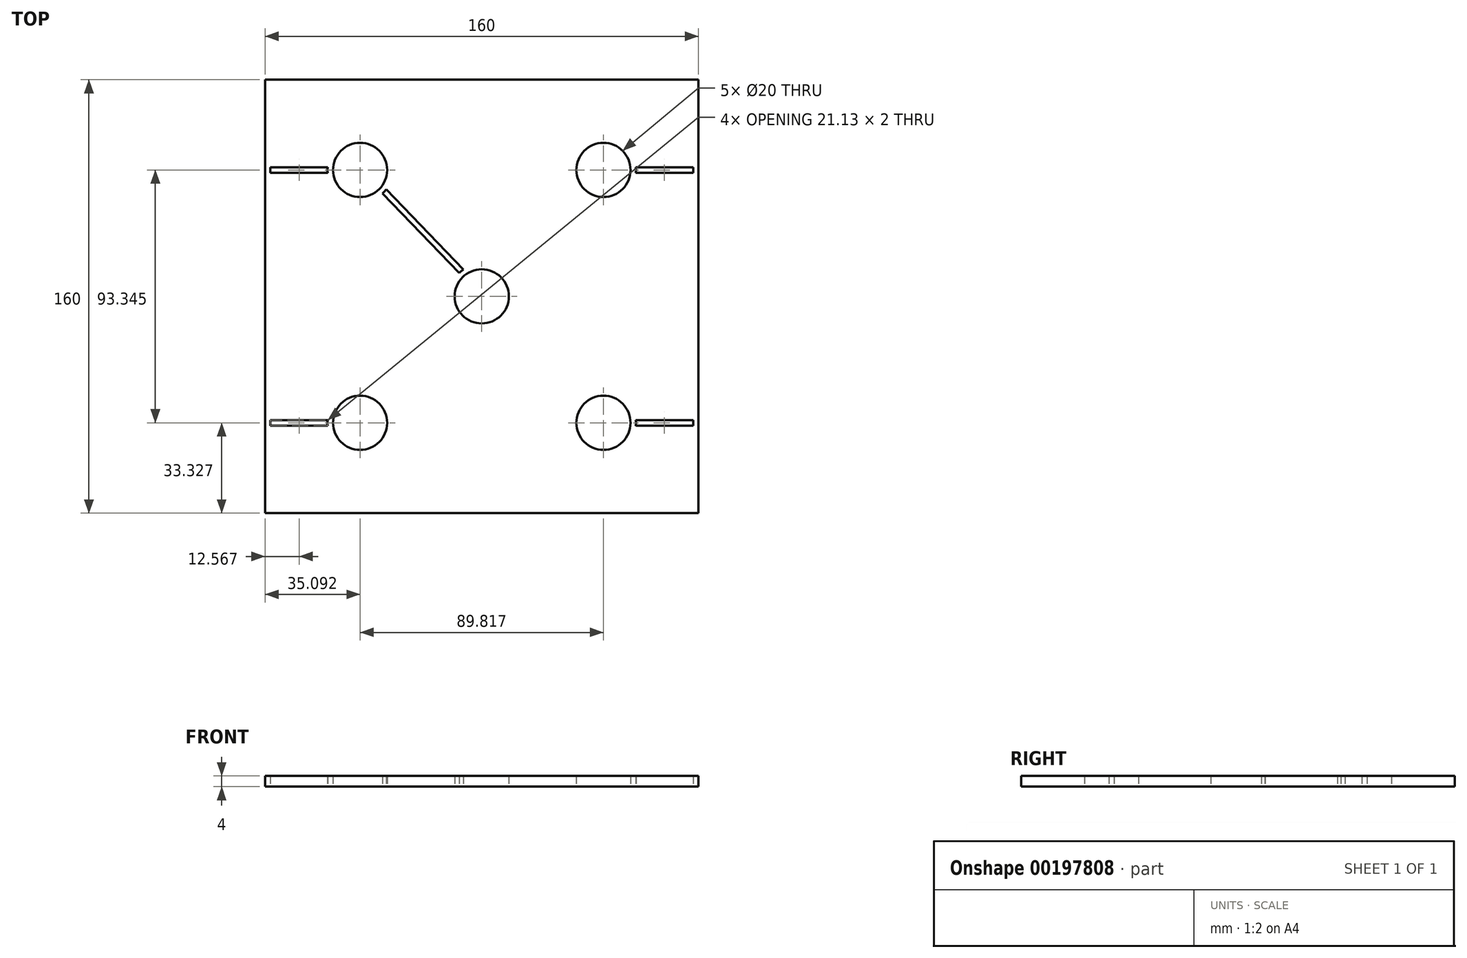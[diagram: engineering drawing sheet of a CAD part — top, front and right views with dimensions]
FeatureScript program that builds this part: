
annotation { "Feature Type Name" : "Feature", "Feature Type Description" : "" }
export const myFeature = defineFeature(function(context is Context, id is Id, definition is map)
    precondition{}
    {
        {
            var Q0;
            Q0=qCreatedBy(makeId("Top.planeOp"),FACE);
            var sketch = newSketch(context, id + "F0", { "sketchPlane" : qUnion([Q0])});
            skLineSegment(sketch, "E0.bottom", {"start": v(80, -80) * mm, "end": v(-80, -80) * mm});
            skLineSegment(sketch, "E0.top", {"start": v(80, 80) * mm, "end": v(-80, 80) * mm});
            skLineSegment(sketch, "E0.left", {"start": v(80, -80) * mm, "end": v(80, 80) * mm});
            skLineSegment(sketch, "E0.right", {"start": v(-80, -80) * mm, "end": v(-80, 80) * mm});
            skPoint(sketch, "E0.middle", {"position": v(0, 0) * mm});
            skLineSegment(sketch, "E1.bottom", {"start": v(78, -78) * mm, "end": v(-78, -78) * mm});
            skLineSegment(sketch, "E1.top", {"start": v(78, 78) * mm, "end": v(-78, 78) * mm});
            skLineSegment(sketch, "E1.left", {"start": v(78, -78) * mm, "end": v(78, 78) * mm});
            skLineSegment(sketch, "E1.right", {"start": v(-78, -78) * mm, "end": v(-78, 78) * mm});
            skCircle(sketch, "E2", {"center": v(0, 0) * mm, "radius": 10 * mm});
            skCircle(sketch, "E3", {"center": v(0, 0) * mm, "radius": 12 * mm});
            skCircle(sketch, "E4", {"center": v(-44.9, -46.67) * mm, "radius": 10 * mm});
            skCircle(sketch, "E5", {"center": v(-44.9, -46.67) * mm, "radius": 12 * mm});
            skCircle(sketch, "E6", {"center": v(44.9, -46.67) * mm, "radius": 10 * mm});
            skCircle(sketch, "E7", {"center": v(44.9, -46.67) * mm, "radius": 12 * mm});
            skCircle(sketch, "E8", {"center": v(44.9, 46.67) * mm, "radius": 10 * mm});
            skCircle(sketch, "E9", {"center": v(44.9, 46.67) * mm, "radius": 12 * mm});
            skCircle(sketch, "E10", {"center": v(-44.9, 46.67) * mm, "radius": 10 * mm});
            skCircle(sketch, "E11", {"center": v(-44.9, 46.67) * mm, "radius": 12 * mm});
            skLineSegment(sketch, "E12", {"start": v(-44.9, -46.67) * mm, "end": v(44.9, 46.67) * mm});
            skLineSegment(sketch, "E13", {"start": v(-44.9, 46.67) * mm, "end": v(44.9, -46.67) * mm});
            skArc(sketch, "E14.0.startCap", {"start": v(-46.35, 45.29) * mm, "mid": v(-46.3, 48.11) * mm, "end": v(-43.47, 48.06) * mm});
            skArc(sketch, "E14.0.endCap", {"start": v(46.35, -45.29) * mm, "mid": v(46.3, -48.11) * mm, "end": v(43.47, -48.06) * mm});
            skLineSegment(sketch, "E14.0.left", {"start": v(-43.47, 48.06) * mm, "end": v(46.35, -45.29) * mm});
            skLineSegment(sketch, "E14.0.right", {"start": v(-46.35, 45.29) * mm, "end": v(43.47, -48.06) * mm});
            skArc(sketch, "E15.0.startCap", {"start": v(-43.47, -48.06) * mm, "mid": v(-46.3, -48.11) * mm, "end": v(-46.35, -45.29) * mm});
            skArc(sketch, "E15.0.endCap", {"start": v(43.47, 48.06) * mm, "mid": v(46.3, 48.11) * mm, "end": v(46.35, 45.29) * mm});
            skLineSegment(sketch, "E15.0.left", {"start": v(-46.35, -45.29) * mm, "end": v(43.47, 48.06) * mm});
            skLineSegment(sketch, "E15.0.right", {"start": v(-43.47, -48.06) * mm, "end": v(46.35, 45.29) * mm});
            skLineSegment(sketch, "E16", {"start": v(0, -78) * mm, "end": v(0, 78) * mm, "construction": true});
            skArc(sketch, "E17.0.endCap", {"start": v(-56.9, 47.67) * mm, "mid": v(-56.89, 47.67) * mm, "end": v(-56.87, 47.67) * mm});
            skLineSegment(sketch, "E17.0.left", {"start": v(-78, 47.67) * mm, "end": v(-56.9, 47.67) * mm});
            skLineSegment(sketch, "E17.0.right", {"start": v(-78, 45.67) * mm, "end": v(-56.9, 45.67) * mm});
            skArc(sketch, "E18.0.endCap", {"start": v(56.9, 45.67) * mm, "mid": v(56.89, 45.67) * mm, "end": v(56.87, 45.67) * mm});
            skLineSegment(sketch, "E18.0.left", {"start": v(78, 45.67) * mm, "end": v(56.9, 45.67) * mm});
            skLineSegment(sketch, "E18.0.right", {"start": v(78, 47.67) * mm, "end": v(56.9, 47.67) * mm});
            skArc(sketch, "E19.0.endCap", {"start": v(56.9, -47.67) * mm, "mid": v(56.89, -47.67) * mm, "end": v(56.87, -47.67) * mm});
            skLineSegment(sketch, "E19.0.left", {"start": v(78, -47.67) * mm, "end": v(56.9, -47.67) * mm});
            skLineSegment(sketch, "E19.0.right", {"start": v(78, -45.67) * mm, "end": v(56.9, -45.67) * mm});
            skArc(sketch, "E20.0.endCap", {"start": v(-56.9, -45.67) * mm, "mid": v(-56.89, -45.67) * mm, "end": v(-56.87, -45.67) * mm});
            skLineSegment(sketch, "E20.0.left", {"start": v(-78, -45.67) * mm, "end": v(-56.9, -45.67) * mm});
            skLineSegment(sketch, "E20.0.right", {"start": v(-78, -47.67) * mm, "end": v(-56.9, -47.67) * mm});
            skArc(sketch, "E21.trimOffspring", {"start": v(-56.87, -47.67) * mm, "mid": v(-56.89, -47.67) * mm, "end": v(-56.9, -47.67) * mm});
            skPoint(sketch, "E22.MirrorCS.start.orphan", {"position": v(-78, -46.67) * mm});
            skArc(sketch, "E23.trimOffspring", {"start": v(56.87, -45.67) * mm, "mid": v(56.89, -45.67) * mm, "end": v(56.9, -45.67) * mm});
            skPoint(sketch, "E19.0.startCap.center.orphan", {"position": v(78, -46.67) * mm});
            skArc(sketch, "E24.trimOffspring", {"start": v(56.87, 47.67) * mm, "mid": v(56.89, 47.67) * mm, "end": v(56.9, 47.67) * mm});
            skPoint(sketch, "E25.start.orphan", {"position": v(78, 46.67) * mm});
            skArc(sketch, "E26.trimOffspring", {"start": v(-56.87, 45.67) * mm, "mid": v(-56.89, 45.67) * mm, "end": v(-56.9, 45.67) * mm});
            skPoint(sketch, "E17.0.startCap.center.orphan", {"position": v(-78, 46.67) * mm});
            skSolve(sketch);
        }
        {
            var Q0;
            Q0=makeQuery(id+"F0.imprint","IMPRINT",FACE,{"disambiguationData":[TD([[makeQuery(id+"F0.imprint","IMPRINT",EDGE,{"derivedFrom":sQuery(id+"F0.wireOp",EDGE,"E0.bottom")}),-1.0]])]});
            var Q1;
            Q1=makeQuery(id+"F0.imprint","IMPRINT",FACE,{"disambiguationData":[TD([[makeQuery(id+"F0.imprint","IMPRINT",EDGE,{"derivedFrom":sQuery(id+"F0.wireOp",EDGE,"E4")}),-1.0]])]});
            var Q2;
            Q2=makeQuery(id+"F0.imprint","IMPRINT",FACE,{"disambiguationData":[TD([[makeQuery(id+"F0.imprint","IMPRINT",EDGE,{"derivedFrom":sQuery(id+"F0.wireOp",EDGE,"E2")}),-1.0]])]});
            var Q3;
            Q3=makeQuery(id+"F0.imprint","IMPRINT",FACE,{"disambiguationData":[TD([[makeQuery(id+"F0.imprint","IMPRINT",EDGE,{"derivedFrom":sQuery(id+"F0.wireOp",EDGE,"E6")}),-1.0]])]});
            var Q4;
            Q4=makeQuery(id+"F0.imprint","IMPRINT",FACE,{"disambiguationData":[TD([[makeQuery(id+"F0.imprint","IMPRINT",EDGE,{"derivedFrom":sQuery(id+"F0.wireOp",EDGE,"E8")}),-1.0]])]});
            var Q5;
            Q5=makeQuery(id+"F0.imprint","IMPRINT",FACE,{"disambiguationData":[TD([[makeQuery(id+"F0.imprint","IMPRINT",EDGE,{"derivedFrom":sQuery(id+"F0.wireOp",EDGE,"E10")}),-1.0]])]});
            var Q6;
            {var subQ0=sQuery(id+"F0.wireOp",EDGE,"E13");var subQ1=sQuery(id+"F0.wireOp",EDGE,"E3");var subQ2=makeQuery(id+"F0.imprint","INTERSECT",VERTEX,{"disambiguationData":[OD(0.0)],"derivedFrom":[subQ1,subQ0]});Q6=makeQuery(id+"F0.imprint","IMPRINT",FACE,{"disambiguationData":[TD([[makeQuery(id+"F0.imprint","IMPRINT",EDGE,{"disambiguationData":[TD([[subQ2,-1.0]])],"derivedFrom":subQ1}),-1.0]])]});}
            var Q7;
            {var subQ0=sQuery(id+"F0.wireOp",EDGE,"E14.0.left");var subQ1=sQuery(id+"F0.wireOp",EDGE,"E3");var subQ2=makeQuery(id+"F0.imprint","INTERSECT",VERTEX,{"disambiguationData":[OD(0.0)],"derivedFrom":[subQ1,subQ0]});Q7=makeQuery(id+"F0.imprint","IMPRINT",FACE,{"disambiguationData":[TD([[makeQuery(id+"F0.imprint","IMPRINT",EDGE,{"disambiguationData":[TD([[subQ2,-1.0]])],"derivedFrom":subQ1}),-1.0]])]});}
            var Q8;
            {var subQ0=sQuery(id+"F0.wireOp",EDGE,"E15.0.left");var subQ1=sQuery(id+"F0.wireOp",EDGE,"E3");var subQ2=makeQuery(id+"F0.imprint","INTERSECT",VERTEX,{"disambiguationData":[OD(1.0)],"derivedFrom":[subQ1,subQ0]});Q8=makeQuery(id+"F0.imprint","IMPRINT",FACE,{"disambiguationData":[TD([[makeQuery(id+"F0.imprint","IMPRINT",EDGE,{"disambiguationData":[TD([[subQ2,-1.0]])],"derivedFrom":subQ1}),-1.0]])]});}
            var Q9;
            {var subQ0=sQuery(id+"F0.wireOp",EDGE,"E12");var subQ1=sQuery(id+"F0.wireOp",EDGE,"E3");var subQ2=makeQuery(id+"F0.imprint","INTERSECT",VERTEX,{"disambiguationData":[OD(1.0)],"derivedFrom":[subQ1,subQ0]});Q9=makeQuery(id+"F0.imprint","IMPRINT",FACE,{"disambiguationData":[TD([[makeQuery(id+"F0.imprint","IMPRINT",EDGE,{"disambiguationData":[TD([[subQ2,-1.0]])],"derivedFrom":subQ1}),-1.0]])]});}
            var Q10;
            {var subQ0=sQuery(id+"F0.wireOp",EDGE,"E14.0.right");var subQ1=sQuery(id+"F0.wireOp",EDGE,"E3");var subQ2=makeQuery(id+"F0.imprint","INTERSECT",VERTEX,{"disambiguationData":[OD(1.0)],"derivedFrom":[subQ1,subQ0]});Q10=makeQuery(id+"F0.imprint","IMPRINT",FACE,{"disambiguationData":[TD([[makeQuery(id+"F0.imprint","IMPRINT",EDGE,{"disambiguationData":[TD([[subQ2,-1.0]])],"derivedFrom":subQ1}),-1.0]])]});}
            var Q11;
            {var subQ0=sQuery(id+"F0.wireOp",EDGE,"E13");var subQ1=sQuery(id+"F0.wireOp",EDGE,"E3");var subQ2=makeQuery(id+"F0.imprint","INTERSECT",VERTEX,{"disambiguationData":[OD(1.0)],"derivedFrom":[subQ1,subQ0]});Q11=makeQuery(id+"F0.imprint","IMPRINT",FACE,{"disambiguationData":[TD([[makeQuery(id+"F0.imprint","IMPRINT",EDGE,{"disambiguationData":[TD([[subQ2,-1.0]])],"derivedFrom":subQ1}),-1.0]])]});}
            var Q12;
            {var subQ0=sQuery(id+"F0.wireOp",EDGE,"E12");var subQ1=sQuery(id+"F0.wireOp",EDGE,"E3");var subQ2=makeQuery(id+"F0.imprint","INTERSECT",VERTEX,{"disambiguationData":[OD(0.0)],"derivedFrom":[subQ1,subQ0]});Q12=makeQuery(id+"F0.imprint","IMPRINT",FACE,{"disambiguationData":[TD([[makeQuery(id+"F0.imprint","IMPRINT",EDGE,{"disambiguationData":[TD([[subQ2,1.0]])],"derivedFrom":subQ1}),-1.0]])]});}
            var Q13;
            {var subQ0=sQuery(id+"F0.wireOp",EDGE,"E12");var subQ1=sQuery(id+"F0.wireOp",EDGE,"E3");var subQ2=makeQuery(id+"F0.imprint","INTERSECT",VERTEX,{"disambiguationData":[OD(0.0)],"derivedFrom":[subQ1,subQ0]});Q13=makeQuery(id+"F0.imprint","IMPRINT",FACE,{"disambiguationData":[TD([[makeQuery(id+"F0.imprint","IMPRINT",EDGE,{"disambiguationData":[TD([[subQ2,-1.0]])],"derivedFrom":subQ1}),-1.0]])]});}
            var Q14;
            {var subQ2=sQuery(id+"F0.wireOp",EDGE,"E17.0.endCap");Q14=makeQuery(id+"F0.imprint","IMPRINT",FACE,{"disambiguationData":[TD([[makeQuery(id+"F0.imprint","IMPRINT",EDGE,{"derivedFrom":subQ2}),-1.0]])]});}
            var Q15;
            {var subQ5=sQuery(id+"F0.wireOp",EDGE,"E14.0.right");var subQ7=sQuery(id+"F0.wireOp",EDGE,"E10");var subQ8=makeQuery(id+"F0.imprint","INTERSECT",VERTEX,{"derivedFrom":[subQ7,subQ5]});Q15=makeQuery(id+"F0.imprint","IMPRINT",FACE,{"disambiguationData":[TD([[makeQuery(id+"F0.imprint","IMPRINT",EDGE,{"disambiguationData":[TD([[subQ8,1.0]])],"derivedFrom":subQ7}),-1.0]])]});}
            var Q16;
            {var subQ5=sQuery(id+"F0.wireOp",EDGE,"E15.0.left");var subQ7=sQuery(id+"F0.wireOp",EDGE,"E8");var subQ8=makeQuery(id+"F0.imprint","INTERSECT",VERTEX,{"derivedFrom":[subQ7,subQ5]});Q16=makeQuery(id+"F0.imprint","IMPRINT",FACE,{"disambiguationData":[TD([[makeQuery(id+"F0.imprint","IMPRINT",EDGE,{"disambiguationData":[TD([[subQ8,1.0]])],"derivedFrom":subQ7}),-1.0]])]});}
            var Q17;
            {var subQ1=sQuery(id+"F0.wireOp",EDGE,"E18.0.endCap");Q17=makeQuery(id+"F0.imprint","IMPRINT",FACE,{"disambiguationData":[TD([[makeQuery(id+"F0.imprint","IMPRINT",EDGE,{"derivedFrom":subQ1}),-1.0]])]});}
            var Q18;
            {var subQ5=sQuery(id+"F0.wireOp",EDGE,"E6");var subQ7=sQuery(id+"F0.wireOp",EDGE,"E14.0.left");var subQ9=makeQuery(id+"F0.imprint","INTERSECT",VERTEX,{"derivedFrom":[subQ5,subQ7]});Q18=makeQuery(id+"F0.imprint","IMPRINT",FACE,{"disambiguationData":[TD([[makeQuery(id+"F0.imprint","IMPRINT",EDGE,{"disambiguationData":[TD([[subQ9,1.0]])],"derivedFrom":subQ5}),-1.0]])]});}
            var Q19;
            {var subQ2=sQuery(id+"F0.wireOp",EDGE,"E19.0.endCap");Q19=makeQuery(id+"F0.imprint","IMPRINT",FACE,{"disambiguationData":[TD([[makeQuery(id+"F0.imprint","IMPRINT",EDGE,{"derivedFrom":subQ2}),-1.0]])]});}
            var Q20;
            {var subQ2=sQuery(id+"F0.wireOp",EDGE,"E15.0.right");var subQ7=sQuery(id+"F0.wireOp",EDGE,"E4");var subQ8=makeQuery(id+"F0.imprint","INTERSECT",VERTEX,{"derivedFrom":[subQ7,subQ2]});Q20=makeQuery(id+"F0.imprint","IMPRINT",FACE,{"disambiguationData":[TD([[makeQuery(id+"F0.imprint","IMPRINT",EDGE,{"disambiguationData":[TD([[subQ8,1.0]])],"derivedFrom":subQ7}),-1.0]])]});}
            var Q21;
            {var subQ3=sQuery(id+"F0.wireOp",EDGE,"E20.0.endCap");Q21=makeQuery(id+"F0.imprint","IMPRINT",FACE,{"disambiguationData":[TD([[makeQuery(id+"F0.imprint","IMPRINT",EDGE,{"derivedFrom":subQ3}),-1.0]])]});}
            extrude(context, id + "F1", {"entities" : qUnion([Q0, Q1, Q2, Q3, Q4, Q5, Q6, Q7, Q8, Q9, Q10, Q11, Q12, Q13, Q14, Q15, Q16, Q17, Q18, Q19, Q20, Q21]), "depth" : 4 * mm});
        }
    });
